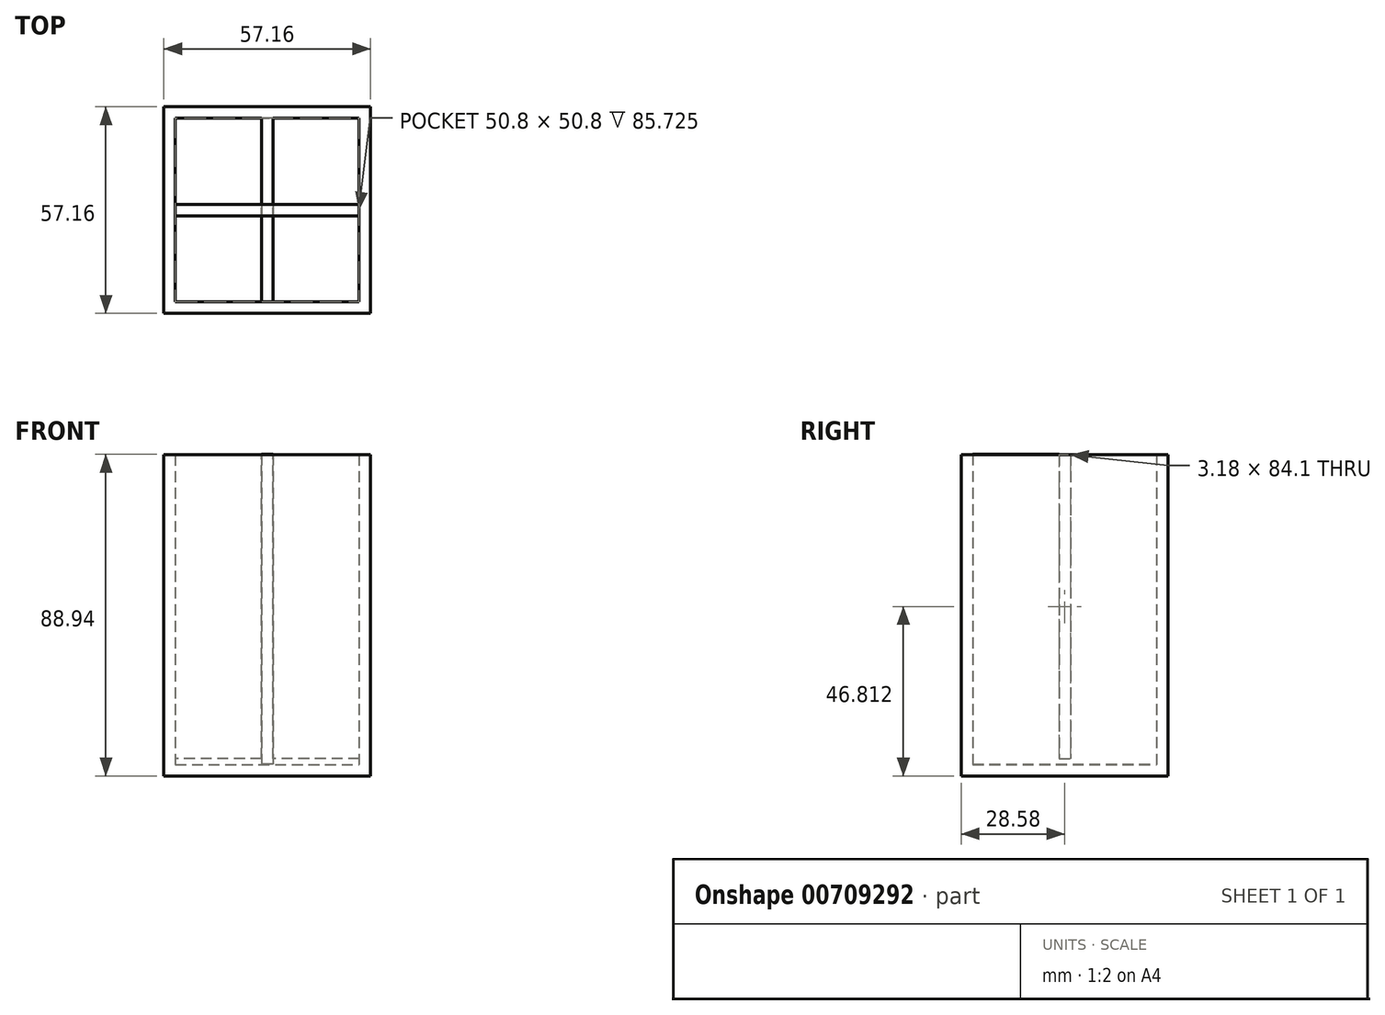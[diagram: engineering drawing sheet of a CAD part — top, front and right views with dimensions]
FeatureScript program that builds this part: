
annotation { "Feature Type Name" : "Feature", "Feature Type Description" : "" }
export const myFeature = defineFeature(function(context is Context, id is Id, definition is map)
    precondition{}
    {
        {
            var Q0;
            Q0=qCreatedBy(makeId("Front.planeOp"),FACE);
            var sketch = newSketch(context, id + "F0", { "sketchPlane" : qUnion([Q0])});
            skLineSegment(sketch, "E0.bottom", {"start": v(25.4, 44.45) * mm, "end": v(-25.4, 44.45) * mm});
            skLineSegment(sketch, "E0.top", {"start": v(25.4, -44.45) * mm, "end": v(-25.4, -44.45) * mm});
            skLineSegment(sketch, "E0.left", {"start": v(25.4, 44.45) * mm, "end": v(25.4, -44.45) * mm});
            skLineSegment(sketch, "E0.right", {"start": v(-25.4, 44.45) * mm, "end": v(-25.4, -44.45) * mm});
            skPoint(sketch, "E0.middle", {"position": v(0, 0) * mm});
            skSolve(sketch);
        }
        {
            var Q0;
            Q0=makeQuery(id+"F0.imprint","IMPRINT",FACE,{"disambiguationData":[TD([[makeQuery(id+"F0.imprint","IMPRINT",EDGE,{"derivedFrom":sQuery(id+"F0.wireOp",EDGE,"E0.bottom")}),1.0]])]});
            extrude(context, id + "F1", {"entities" : qUnion([Q0]), "depth" : 3.17 * mm, "offsetDistance" : 25.4 * mm});
        }
        {
            var Q0;
            Q0=makeQuery(id+"F1.opExtrude","SWEPT_FACE",FACE,{"disambiguationData":[OSD([sQuery(id+"F0.wireOp",EDGE,"E0.left")])]});
            var sketch = newSketch(context, id + "F2", { "sketchPlane" : qUnion([Q0])});
            skLineSegment(sketch, "E1.bottom", {"start": v(-3.17, 44.45) * mm, "end": v(53.98, 44.45) * mm});
            skLineSegment(sketch, "E1.top", {"start": v(-3.17, -44.45) * mm, "end": v(53.98, -44.45) * mm});
            skLineSegment(sketch, "E1.left", {"start": v(-3.18, 44.45) * mm, "end": v(-3.18, -44.45) * mm});
            skLineSegment(sketch, "E1.right", {"start": v(53.98, 44.45) * mm, "end": v(53.98, -44.45) * mm});
            skSolve(sketch);
        }
        {
            var Q0;
            Q0 = qSketchRegion(id + "F2", true);
            extrude(context, id + "F3", {"entities" : qUnion([Q0]), "operationType" : NewBodyOperationType.ADD, "depth" : 3.17 * mm, "offsetDistance" : 25.4 * mm});
        }
        {
            var Q0;
            Q0=makeQuery(id+"F3.opExtrude","SWEPT_FACE",FACE,{"disambiguationData":[OSD([sQuery(id+"F2.wireOp",EDGE,"E1.right")])]});
            cPlane(context, id + "F4", {"entities" : qUnion([Q0]), "cplaneType" : CPlaneType.OFFSET, "offset" : 3.17 * mm, "oppositeDirection" : true, "width" : 152.4 * mm, "height" : 152.4 * mm});
        }
        {
            var Q0;
            Q0=qCreatedBy(id+"F4.planeOp",FACE);
            var sketch = newSketch(context, id + "F5", { "sketchPlane" : qUnion([Q0])});
            skLineSegment(sketch, "E2.bottom", {"start": v(25.4, 44.45) * mm, "end": v(-25.4, 44.45) * mm});
            skLineSegment(sketch, "E2.top", {"start": v(25.4, -44.45) * mm, "end": v(-25.4, -44.45) * mm});
            skLineSegment(sketch, "E2.left", {"start": v(25.4, 44.45) * mm, "end": v(25.4, -44.45) * mm});
            skLineSegment(sketch, "E2.right", {"start": v(-25.4, 44.45) * mm, "end": v(-25.4, -44.45) * mm});
            skPoint(sketch, "E2.middle", {"position": v(0, 0) * mm});
            skSolve(sketch);
        }
        {
            var Q0;
            Q0 = qSketchRegion(id + "F5", true);
            extrude(context, id + "F6", {"entities" : qUnion([Q0]), "operationType" : NewBodyOperationType.ADD, "depth" : 3.17 * mm, "offsetDistance" : 25.4 * mm});
        }
        {
            var Q0;
            Q0=makeQuery(id+"F6.opExtrude","SWEPT_FACE",FACE,{"disambiguationData":[OSD([sQuery(id+"F5.wireOp",EDGE,"E2.left")])]});
            var sketch = newSketch(context, id + "F7", { "sketchPlane" : qUnion([Q0])});
            skLineSegment(sketch, "E3.bottom", {"start": v(-53.97, 44.45) * mm, "end": v(3.17, 44.45) * mm});
            skLineSegment(sketch, "E3.top", {"start": v(-53.98, -44.45) * mm, "end": v(3.18, -44.45) * mm});
            skLineSegment(sketch, "E3.left", {"start": v(-53.98, 44.45) * mm, "end": v(-53.98, -44.45) * mm});
            skLineSegment(sketch, "E3.right", {"start": v(3.17, 44.45) * mm, "end": v(3.17, -44.45) * mm});
            skSolve(sketch);
        }
        {
            var Q0;
            Q0 = qSketchRegion(id + "F7", true);
            extrude(context, id + "F8", {"entities" : qUnion([Q0]), "operationType" : NewBodyOperationType.ADD, "depth" : 3.17 * mm, "offsetDistance" : 25.4 * mm});
        }
        {
            var Q0;
            Q0=makeQuery(id+"F8.boolean.opBoolean","MERGE",FACE,{"derivedFrom":[makeQuery(id+"F6.boolean.opBoolean","MERGE",FACE,{"derivedFrom":[makeQuery(id+"F3.boolean.opBoolean","MERGE",FACE,{"derivedFrom":[makeQuery(id+"F1.opExtrude","SWEPT_FACE",FACE,{"disambiguationData":[OSD([sQuery(id+"F0.wireOp",EDGE,"E0.top")])]}),makeQuery(id+"F3.opExtrude","SWEPT_FACE",FACE,{"disambiguationData":[OSD([sQuery(id+"F2.wireOp",EDGE,"E1.top")])]})]}),makeQuery(id+"F6.opExtrude","SWEPT_FACE",FACE,{"disambiguationData":[OSD([sQuery(id+"F5.wireOp",EDGE,"E2.top")])]})]}),makeQuery(id+"F8.opExtrude","SWEPT_FACE",FACE,{"disambiguationData":[OSD([sQuery(id+"F7.wireOp",EDGE,"E3.top")])]})]});
            cPlane(context, id + "F9", {"entities" : qUnion([Q0]), "cplaneType" : CPlaneType.OFFSET, "offset" : 3.17 * mm, "oppositeDirection" : true, "width" : 152.4 * mm, "height" : 152.4 * mm});
        }
        {
            var Q0;
            Q0=qCreatedBy(id+"F9.planeOp",FACE);
            var sketch = newSketch(context, id + "F10", { "sketchPlane" : qUnion([Q0])});
            skLineSegment(sketch, "E4.bottom", {"start": v(-25.4, 0) * mm, "end": v(25.4, 0) * mm});
            skLineSegment(sketch, "E4.top", {"start": v(-25.4, -50.8) * mm, "end": v(25.4, -50.8) * mm});
            skLineSegment(sketch, "E4.left", {"start": v(-25.4, 0) * mm, "end": v(-25.4, -50.8) * mm});
            skLineSegment(sketch, "E4.right", {"start": v(25.4, 0) * mm, "end": v(25.4, -50.8) * mm});
            skSolve(sketch);
        }
        {
            var Q0;
            Q0 = qSketchRegion(id + "F10", true);
            extrude(context, id + "F11", {"entities" : qUnion([Q0]), "operationType" : NewBodyOperationType.ADD, "depth" : 3.17 * mm, "offsetDistance" : 25.4 * mm});
        }
        {
            var Q0;
            Q0=makeQuery(id+"F6.opExtrude","CAP_FACE",FACE,{"disambiguationData":[OSD([sQuery(id+"F5.wireOp",EDGE,"E2.bottom"),sQuery(id+"F5.wireOp",EDGE,"E2.top"),sQuery(id+"F5.wireOp",EDGE,"E2.left"),sQuery(id+"F5.wireOp",EDGE,"E2.right")])],"isStart":true});
            cPlane(context, id + "F12", {"entities" : qUnion([Q0]), "cplaneType" : CPlaneType.OFFSET, "offset" : 23.8 * mm, "width" : 152.4 * mm, "height" : 152.4 * mm});
        }
        {
            var Q0;
            Q0=qCreatedBy(id+"F12.planeOp",FACE);
            var sketch = newSketch(context, id + "F13", { "sketchPlane" : qUnion([Q0])});
            skLineSegment(sketch, "E5.bottom", {"start": v(25.4, 39.69) * mm, "end": v(-25.4, 39.69) * mm});
            skLineSegment(sketch, "E5.top", {"start": v(25.4, -39.69) * mm, "end": v(-25.4, -39.69) * mm});
            skLineSegment(sketch, "E5.left", {"start": v(25.4, 39.69) * mm, "end": v(25.4, -39.69) * mm});
            skLineSegment(sketch, "E5.right", {"start": v(-25.4, 39.69) * mm, "end": v(-25.4, -39.69) * mm});
            skPoint(sketch, "E5.middle", {"position": v(0, 0) * mm});
            skSolve(sketch);
        }
        {
            var Q0;
            Q0 = qSketchRegion(id + "F13", true);
            extrude(context, id + "F14", {"entities" : qUnion([Q0]), "operationType" : NewBodyOperationType.ADD, "depth" : 3.17 * mm, "offsetDistance" : 25.4 * mm});
        }
        {
            var Q0;
            Q0=makeQuery(id+"F8.opExtrude","CAP_FACE",FACE,{"disambiguationData":[OSD([sQuery(id+"F7.wireOp",EDGE,"E3.bottom"),sQuery(id+"F7.wireOp",EDGE,"E3.top"),sQuery(id+"F7.wireOp",EDGE,"E3.left"),sQuery(id+"F7.wireOp",EDGE,"E3.right")])],"isStart":true});
            cPlane(context, id + "F15", {"entities" : qUnion([Q0]), "cplaneType" : CPlaneType.OFFSET, "offset" : 23.8 * mm, "width" : 152.4 * mm, "height" : 152.4 * mm});
        }
        {
            var Q0;
            Q0=qCreatedBy(id+"F15.planeOp",FACE);
            var sketch = newSketch(context, id + "F16", { "sketchPlane" : qUnion([Q0])});
            skLineSegment(sketch, "E6.bottom", {"start": v(0, 38.24) * mm, "end": v(50.8, 38.24) * mm});
            skLineSegment(sketch, "E6.top", {"start": v(0, -41.14) * mm, "end": v(50.8, -41.14) * mm});
            skLineSegment(sketch, "E6.left", {"start": v(0, 38.24) * mm, "end": v(0, -41.14) * mm});
            skLineSegment(sketch, "E6.right", {"start": v(50.8, 38.24) * mm, "end": v(50.8, -41.14) * mm});
            skSolve(sketch);
        }
        {
            var Q0;
            Q0 = qSketchRegion(id + "F16", true);
            extrude(context, id + "F17", {"entities" : qUnion([Q0]), "operationType" : NewBodyOperationType.ADD, "depth" : 3.17 * mm, "offsetDistance" : 25.4 * mm});
        }
        {
            var Q0;
            {var subQ3=sQuery(id+"F16.wireOp",EDGE,"E6.bottom");Q0=makeQuery(id+"F17.boolean.opBoolean","SPLIT",FACE,{"disambiguationData":[TD([makeQuery(id+"F6.opExtrude","CAP_FACE",FACE,{"disambiguationData":[OSD([sQuery(id+"F5.wireOp",EDGE,"E2.bottom"),sQuery(id+"F5.wireOp",EDGE,"E2.top"),sQuery(id+"F5.wireOp",EDGE,"E2.left"),sQuery(id+"F5.wireOp",EDGE,"E2.right")])],"isStart":true})])],"derivedFrom":makeQuery(id+"F17.opExtrude","SWEPT_FACE",FACE,{"disambiguationData":[OSD([subQ3])]})});}
            var sketch = newSketch(context, id + "F18", { "sketchPlane" : qUnion([Q0])});
            skLineSegment(sketch, "E7.bottom", {"start": v(-1.59, 50.8) * mm, "end": v(1.59, 50.8) * mm});
            skLineSegment(sketch, "E7.top", {"start": v(-1.59, 26.99) * mm, "end": v(1.59, 26.99) * mm});
            skLineSegment(sketch, "E7.left", {"start": v(-1.59, 50.8) * mm, "end": v(-1.59, 26.99) * mm});
            skLineSegment(sketch, "E7.right", {"start": v(1.59, 50.8) * mm, "end": v(1.59, 26.99) * mm});
            skSolve(sketch);
        }
        {
            var Q0;
            Q0 = qSketchRegion(id + "F18", true);
            extrude(context, id + "F19", {"entities" : qUnion([Q0]), "operationType" : NewBodyOperationType.ADD, "depth" : 6.22 * mm, "offsetDistance" : 25.4 * mm});
        }
        {
            var Q0;
            {var subQ3=sQuery(id+"F16.wireOp",EDGE,"E6.bottom");Q0=makeQuery(id+"F17.boolean.opBoolean","SPLIT",FACE,{"disambiguationData":[TD([makeQuery(id+"F1.opExtrude","CAP_FACE",FACE,{"disambiguationData":[OSD([sQuery(id+"F0.wireOp",EDGE,"E0.bottom"),sQuery(id+"F0.wireOp",EDGE,"E0.top"),sQuery(id+"F0.wireOp",EDGE,"E0.left"),sQuery(id+"F0.wireOp",EDGE,"E0.right")])],"isStart":true})])],"derivedFrom":makeQuery(id+"F17.opExtrude","SWEPT_FACE",FACE,{"disambiguationData":[OSD([subQ3])]})});}
            var sketch = newSketch(context, id + "F20", { "sketchPlane" : qUnion([Q0])});
            skLineSegment(sketch, "E8.bottom", {"start": v(-1.59, 23.81) * mm, "end": v(1.59, 23.81) * mm});
            skLineSegment(sketch, "E8.top", {"start": v(-1.59, 0) * mm, "end": v(1.59, 0) * mm});
            skLineSegment(sketch, "E8.left", {"start": v(-1.59, 23.81) * mm, "end": v(-1.59, 0) * mm});
            skLineSegment(sketch, "E8.right", {"start": v(1.59, 23.81) * mm, "end": v(1.59, 0) * mm});
            skSolve(sketch);
        }
        {
            var Q0;
            Q0 = qSketchRegion(id + "F20", true);
            extrude(context, id + "F21", {"entities" : qUnion([Q0]), "operationType" : NewBodyOperationType.ADD, "depth" : 6.25 * mm, "offsetDistance" : 25.4 * mm});
        }
        {
            var Q0;
            Q0=makeQuery(id+"F14.opExtrude","SWEPT_FACE",FACE,{"disambiguationData":[OSD([sQuery(id+"F13.wireOp",EDGE,"E5.bottom")])]});
            var sketch = newSketch(context, id + "F22", { "sketchPlane" : qUnion([Q0])});
            skLineSegment(sketch, "E9.bottom", {"start": v(-25.4, 26.99) * mm, "end": v(25.4, 26.99) * mm});
            skLineSegment(sketch, "E9.top", {"start": v(-25.4, 23.81) * mm, "end": v(25.4, 23.81) * mm});
            skLineSegment(sketch, "E9.left", {"start": v(-25.4, 26.99) * mm, "end": v(-25.4, 23.81) * mm});
            skLineSegment(sketch, "E9.right", {"start": v(25.4, 26.99) * mm, "end": v(25.4, 23.81) * mm});
            skSolve(sketch);
        }
        {
            var Q0;
            Q0 = qSketchRegion(id + "F22", true);
            extrude(context, id + "F23", {"entities" : qUnion([Q0]), "operationType" : NewBodyOperationType.ADD, "depth" : 4.72 * mm, "offsetDistance" : 25.4 * mm});
        }
    });
